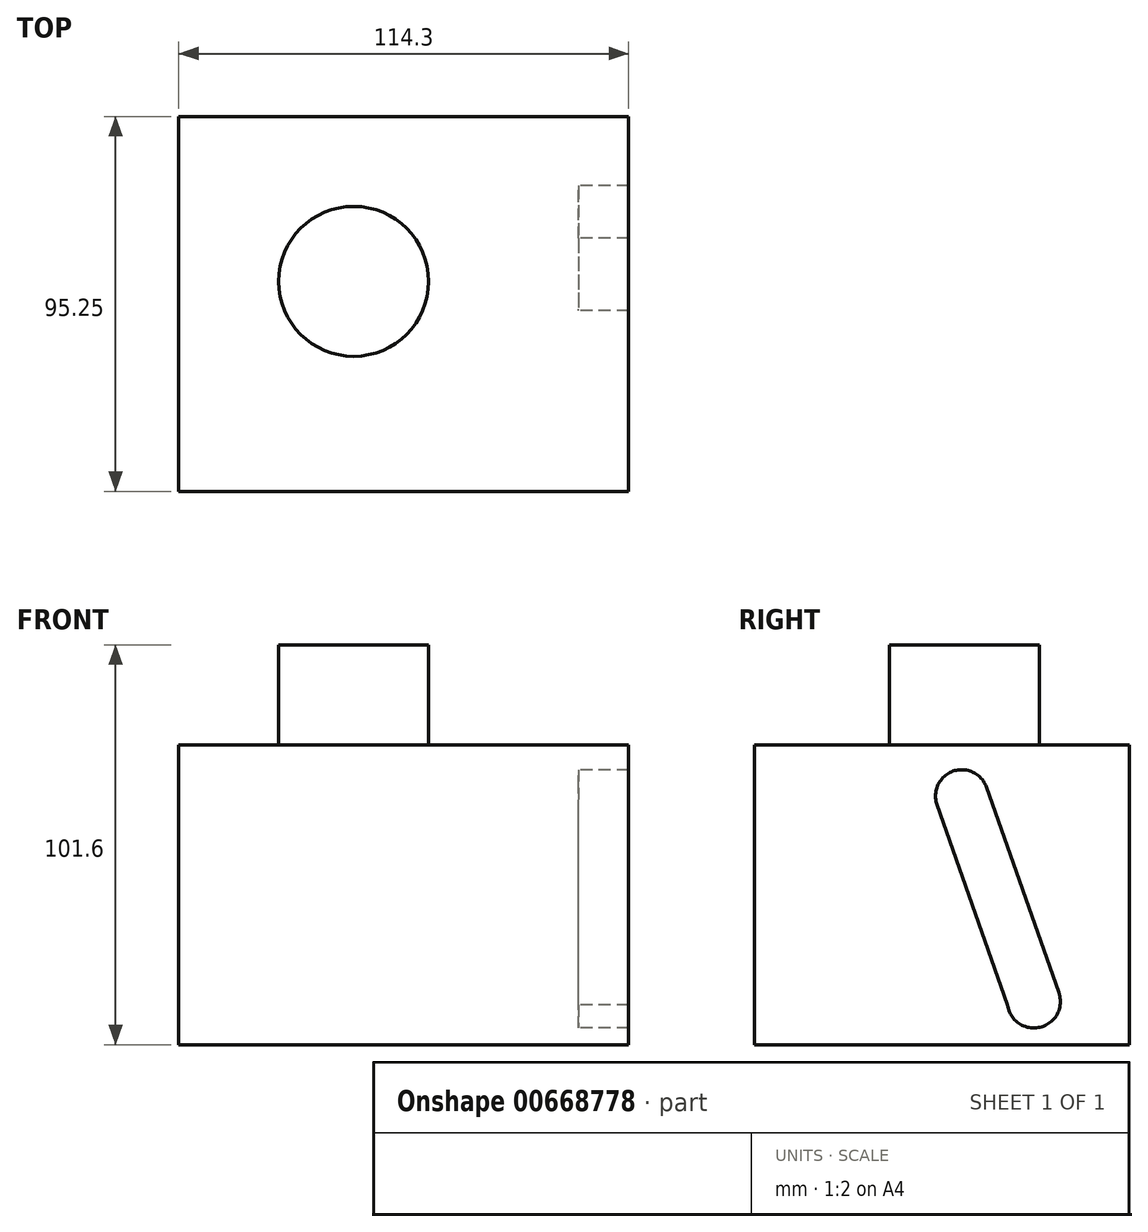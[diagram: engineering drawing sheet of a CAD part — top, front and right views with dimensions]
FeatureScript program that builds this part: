
annotation { "Feature Type Name" : "Feature", "Feature Type Description" : "" }
export const myFeature = defineFeature(function(context is Context, id is Id, definition is map)
    precondition{}
    {
        {
            var Q0;
            Q0=qCreatedBy(makeId("Top.planeOp"),FACE);
            var sketch = newSketch(context, id + "F0", { "sketchPlane" : qUnion([Q0])});
            skLineSegment(sketch, "E0.bottom", {"start": v(0, 0) * mm, "end": v(101.6, 0) * mm});
            skLineSegment(sketch, "E0.top", {"start": v(0, 95.25) * mm, "end": v(101.6, 95.25) * mm});
            skLineSegment(sketch, "E0.left", {"start": v(0, 0) * mm, "end": v(0, 95.25) * mm});
            skLineSegment(sketch, "E0.right", {"start": v(101.6, 0) * mm, "end": v(101.6, 95.25) * mm});
            skSolve(sketch);
        }
        {
            var Q0;
            Q0 = qSketchRegion(id + "F0", true);
            extrude(context, id + "F1", {"entities" : qUnion([Q0]), "depth" : 38.1 * mm, "offsetDistance" : 25.4 * mm, "hasSecondDirection" : true, "secondDirectionOppositeDirection" : true, "secondDirectionDepth" : 38.1 * mm});
        }
        {
            var Q0;
            Q0=makeQuery(id+"F1.opExtrude","CAP_FACE",FACE,{"disambiguationData":[OSD([sQuery(id+"F0.wireOp",EDGE,"E0.bottom"),sQuery(id+"F0.wireOp",EDGE,"E0.top"),sQuery(id+"F0.wireOp",EDGE,"E0.left"),sQuery(id+"F0.wireOp",EDGE,"E0.right")])],"isStart":false});
            var sketch = newSketch(context, id + "F2", { "sketchPlane" : qUnion([Q0])});
            skCircle(sketch, "E1", {"center": v(44.45, 53.34) * mm, "radius": 19.05 * mm});
            skSolve(sketch);
        }
        {
            var Q0;
            Q0 = qSketchRegion(id + "F2", true);
            extrude(context, id + "F3", {"entities" : qUnion([Q0]), "operationType" : NewBodyOperationType.ADD, "depth" : 25.4 * mm, "offsetDistance" : 25.4 * mm});
        }
        {
            var Q0;
            Q0=makeQuery(id+"F1.opExtrude","SWEPT_FACE",FACE,{"disambiguationData":[OSD([sQuery(id+"F0.wireOp",EDGE,"E0.right")])]});
            var sketch = newSketch(context, id + "F4", { "sketchPlane" : qUnion([Q0])});
            skArc(sketch, "E2", {"start": v(58.89, 27.32) * mm, "mid": v(50.4, 31.38) * mm, "end": v(46.34, 22.9) * mm});
            skArc(sketch, "E3", {"start": v(64.28, -27.98) * mm, "mid": v(72.52, -33.67) * mm, "end": v(77.28, -24.86) * mm});
            skLineSegment(sketch, "E4", {"start": v(65.23, -30.66) * mm, "end": v(46.34, 22.9) * mm});
            skLineSegment(sketch, "E5", {"start": v(77.3, -24.95) * mm, "end": v(58.89, 27.32) * mm});
            skSolve(sketch);
        }
        {
            var Q0;
            {var subQ1=sQuery(id+"F4.wireOp",EDGE,"E2");Q0=makeQuery(id+"F4.imprint","IMPRINT",FACE,{"disambiguationData":[TD([[makeQuery(id+"F4.imprint","IMPRINT",EDGE,{"derivedFrom":subQ1}),-1.0]])]});}
            extrude(context, id + "F5", {"entities" : qUnion([Q0]), "operationType" : NewBodyOperationType.ADD, "depth" : 12.7 * mm, "offsetDistance" : 25.4 * mm});
        }
    });
